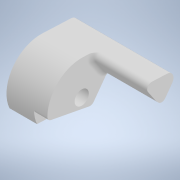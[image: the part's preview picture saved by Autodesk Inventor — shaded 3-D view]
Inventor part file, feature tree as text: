
AUTODESK INVENTOR PART (.ipt)
format: ipt  version: 2022 (Build 260153000, 153)  size: 195,584 bytes
history: native  units: mm
features: other x7, reference x5, extrude x3, fillet x3, sketch x3, projected_geometry x3
ambient origin geometry x8: Origin, YZ Plane, XZ Plane, XY Plane, X Axis, Y Axis, Z Axis, Center Point
bodies: Body1 (feature_tree)
feature tree (24):
  other  "Твердое тело1"
  extrude  "Выдавливание1"  Depth=3.2mm
  other  "РабПлоскость1"
  extrude  "Выдавливание2"  Depth=0.5mm
  fillet  "Сопряжение1"  Radius=3.0mm
  extrude  "Выдавливание3"  Depth=6.2mm TaperAngle=0.0deg
  fillet  "Сопряжение3"  Radius=2.0mm
  fillet  "Сопряжение4"  Radius=10.0mm
  sketch  "Эскиз1"
  reference  "Ссылка1"
  reference  "Ссылка2"
  sketch  "Эскиз2"
  projected_geometry  "Спроецированная петля1"
  reference  "Ссылка3"
  reference  "Ссылка4"
  sketch  "Эскиз3"
  reference  "Ссылка5"
  projected_geometry  "Спроецированная петля2"
  projected_geometry  "Спроецированная петля3"
  other  "<userpath>\Documents\Git\MZCAT_2024\MZCAT_3.iam"
  other  "MZCAT_3.iam"
  other  "base:1"
  other  "base plate:2"
  other  "Linit Switch:2"
